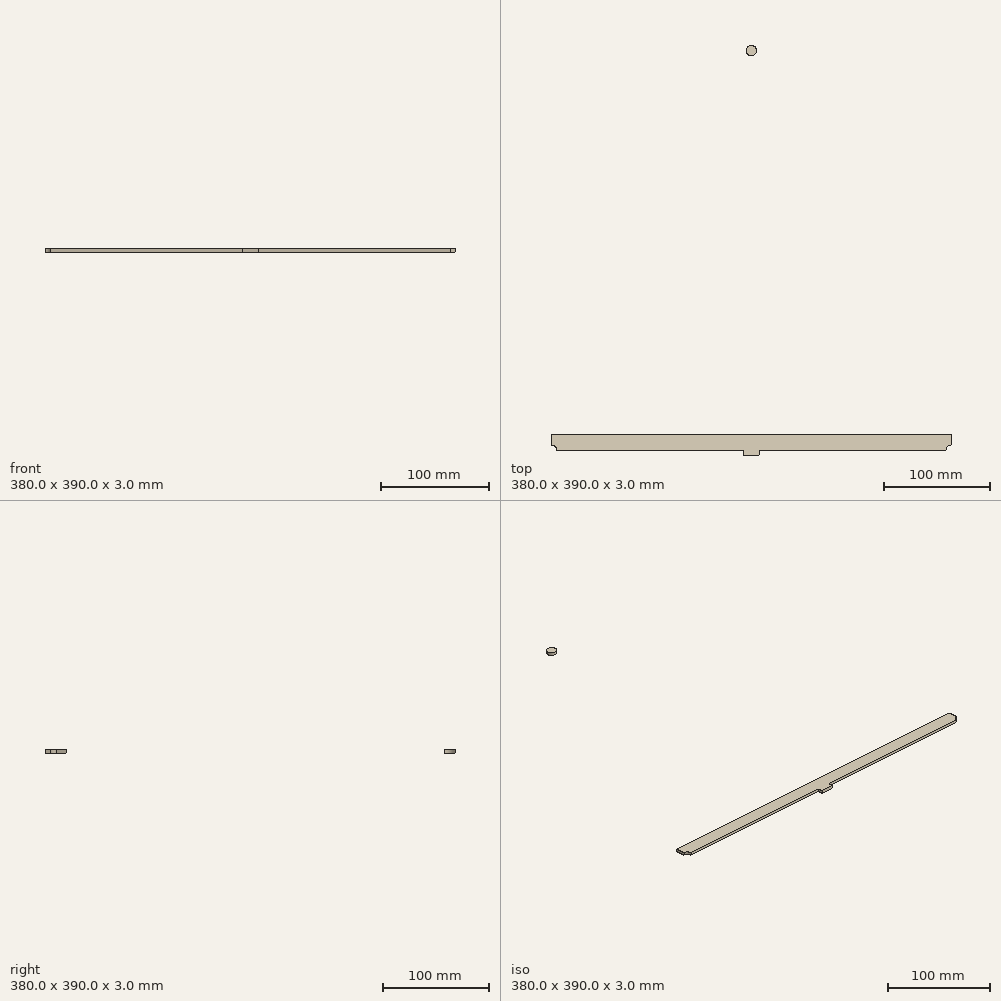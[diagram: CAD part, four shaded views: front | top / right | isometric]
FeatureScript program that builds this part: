
annotation { "Feature Type Name" : "Feature", "Feature Type Description" : "" }
export const myFeature = defineFeature(function(context is Context, id is Id, definition is map)
    precondition{}
    {
        {
            var Q0;
            Q0=qCreatedBy(makeId("Top.planeOp"),FACE);
            var sketch = newSketch(context, id + "F0", { "sketchPlane" : qUnion([Q0])});
            skLineSegment(sketch, "E0.bottom", {"start": v(240, -240) * mm, "end": v(-240, -240) * mm});
            skLineSegment(sketch, "E0.top", {"start": v(240, 240) * mm, "end": v(-240, 240) * mm});
            skLineSegment(sketch, "E0.left", {"start": v(240, -240) * mm, "end": v(240, 240) * mm});
            skLineSegment(sketch, "E0.right", {"start": v(-240, -240) * mm, "end": v(-240, 240) * mm});
            skPoint(sketch, "E0.middle", {"position": v(0, 0) * mm});
            skSolve(sketch);
        }
        {
            var Q0;
            Q0=makeQuery(id+"F0.imprint","IMPRINT",FACE,{"disambiguationData":[TD([[makeQuery(id+"F0.imprint","IMPRINT",EDGE,{"derivedFrom":sQuery(id+"F0.wireOp",EDGE,"E0.bottom")}),-1.0]])]});
            extrude(context, id + "F1", {"entities" : qUnion([Q0]), "depth" : 3 * mm, "offsetDistance" : 25 * mm});
        }
        {
            var Q0;
            Q0=makeQuery(id+"F1.opExtrude","CAP_FACE",FACE,{"disambiguationData":[OSD([sQuery(id+"F0.wireOp",EDGE,"E0.bottom"),sQuery(id+"F0.wireOp",EDGE,"E0.top"),sQuery(id+"F0.wireOp",EDGE,"E0.left"),sQuery(id+"F0.wireOp",EDGE,"E0.right")])],"isStart":false});
            var sketch = newSketch(context, id + "F2", { "sketchPlane" : qUnion([Q0])});
            skLineSegment(sketch, "E1.bottom", {"start": v(-240, 240) * mm, "end": v(-200, 240) * mm});
            skLineSegment(sketch, "E1.top", {"start": v(-240, 200) * mm, "end": v(-200, 200) * mm});
            skLineSegment(sketch, "E1.left", {"start": v(-240, 240) * mm, "end": v(-240, 200) * mm});
            skLineSegment(sketch, "E1.right", {"start": v(-200, 240) * mm, "end": v(-200, 200) * mm});
            skLineSegment(sketch, "E2.bottom", {"start": v(240, 240) * mm, "end": v(200, 240) * mm});
            skLineSegment(sketch, "E2.top", {"start": v(240, 200) * mm, "end": v(200, 200) * mm});
            skLineSegment(sketch, "E2.left", {"start": v(240, 240) * mm, "end": v(240, 200) * mm});
            skLineSegment(sketch, "E2.right", {"start": v(200, 240) * mm, "end": v(200, 200) * mm});
            skLineSegment(sketch, "E3.bottom", {"start": v(240, -240) * mm, "end": v(200, -240) * mm});
            skLineSegment(sketch, "E3.top", {"start": v(240, -200) * mm, "end": v(200, -200) * mm});
            skLineSegment(sketch, "E3.left", {"start": v(240, -240) * mm, "end": v(240, -200) * mm});
            skLineSegment(sketch, "E3.right", {"start": v(200, -240) * mm, "end": v(200, -200) * mm});
            skLineSegment(sketch, "E4.bottom", {"start": v(-240, -240) * mm, "end": v(-200, -240) * mm});
            skLineSegment(sketch, "E4.top", {"start": v(-240, -200) * mm, "end": v(-200, -200) * mm});
            skLineSegment(sketch, "E4.left", {"start": v(-240, -240) * mm, "end": v(-240, -200) * mm});
            skLineSegment(sketch, "E4.right", {"start": v(-200, -240) * mm, "end": v(-200, -200) * mm});
            skSolve(sketch);
        }
        {
            var Q0;
            Q0=qSketchRegion(id+"F2",true);
            extrude(context, id + "F3", {"entities" : qUnion([Q0]), "operationType" : NewBodyOperationType.REMOVE, "oppositeDirection" : true, "depth" : 25 * mm, "offsetDistance" : 25 * mm});
        }
        {
            var Q0;
            Q0=makeQuery(id+"F1.opExtrude","CAP_FACE",FACE,{"disambiguationData":[OSD([sQuery(id+"F0.wireOp",EDGE,"E0.bottom"),sQuery(id+"F0.wireOp",EDGE,"E0.top"),sQuery(id+"F0.wireOp",EDGE,"E0.left"),sQuery(id+"F0.wireOp",EDGE,"E0.right")])],"isStart":false});
            var sketch = newSketch(context, id + "F4", { "sketchPlane" : qUnion([Q0])});
            skLineSegment(sketch, "E5.bottom", {"start": v(-190, -190) * mm, "end": v(190, -190) * mm});
            skLineSegment(sketch, "E5.top", {"start": v(-190, 190) * mm, "end": v(190, 190) * mm});
            skLineSegment(sketch, "E5.left", {"start": v(-190, -190) * mm, "end": v(-190, 190) * mm});
            skLineSegment(sketch, "E5.right", {"start": v(190, -190) * mm, "end": v(190, 190) * mm});
            skPoint(sketch, "E6", {"position": v(0, 190) * mm});
            skPoint(sketch, "E7", {"position": v(-190, -190) * mm});
            skPoint(sketch, "E8", {"position": v(190, -190) * mm});
            skCircle(sketch, "E9", {"center": v(0, 190) * mm, "radius": 5 * mm});
            skCircle(sketch, "E10", {"center": v(-190, -190) * mm, "radius": 5 * mm});
            skCircle(sketch, "E11", {"center": v(190, -190) * mm, "radius": 5 * mm});
            skPoint(sketch, "E12", {"position": v(0, -190) * mm});
            skLineSegment(sketch, "E13.bottom", {"start": v(7.5, -190) * mm, "end": v(-7.5, -190) * mm});
            skLineSegment(sketch, "E13.top", {"start": v(7.5, -190) * mm, "end": v(-7.5, -190) * mm});
            skLineSegment(sketch, "E13.left", {"start": v(7.5, -190) * mm, "end": v(7.5, -190) * mm});
            skLineSegment(sketch, "E13.right", {"start": v(-7.5, -190) * mm, "end": v(-7.5, -190) * mm});
            skPoint(sketch, "E14", {"position": v(-7.5, -190) * mm});
            skPoint(sketch, "E15", {"position": v(7.5, -190) * mm});
            skLineSegment(sketch, "E16.bottom", {"start": v(-7.5, -190) * mm, "end": v(7.5, -190) * mm});
            skLineSegment(sketch, "E16.top", {"start": v(-7.5, -195) * mm, "end": v(7.5, -195) * mm});
            skLineSegment(sketch, "E16.left", {"start": v(-7.5, -190) * mm, "end": v(-7.5, -195) * mm});
            skLineSegment(sketch, "E16.right", {"start": v(7.5, -190) * mm, "end": v(7.5, -195) * mm});
            skLineSegment(sketch, "E17.bottom", {"start": v(200, -175) * mm, "end": v(-200, -175) * mm});
            skLineSegment(sketch, "E17.top", {"start": v(200, 175) * mm, "end": v(-200, 175) * mm});
            skLineSegment(sketch, "E17.left", {"start": v(200, -175) * mm, "end": v(200, 175) * mm});
            skLineSegment(sketch, "E17.right", {"start": v(-200, -175) * mm, "end": v(-200, 175) * mm});
            skPoint(sketch, "E17.middle", {"position": v(0, 0) * mm});
            skSolve(sketch);
        }
        {
            var Q0;
            {var subQ0=sQuery(id+"F4.wireOp",EDGE,"E9");var subQ1=sQuery(id+"F4.wireOp",EDGE,"E5.top");var subQ2=makeQuery(id+"F4.imprint","INTERSECT",VERTEX,{"disambiguationData":[OD(0.0)],"derivedFrom":[subQ1,subQ0]});Q0=makeQuery(id+"F4.imprint","IMPRINT",FACE,{"disambiguationData":[TD([[makeQuery(id+"F4.imprint","IMPRINT",EDGE,{"disambiguationData":[TD([[subQ2,-1.0]])],"derivedFrom":subQ1}),-1.0]])]});}
            var Q1;
            {var subQ0=sQuery(id+"F4.wireOp",EDGE,"E9");var subQ1=sQuery(id+"F4.wireOp",EDGE,"E5.top");var subQ2=makeQuery(id+"F4.imprint","INTERSECT",VERTEX,{"disambiguationData":[OD(0.0)],"derivedFrom":[subQ1,subQ0]});Q1=makeQuery(id+"F4.imprint","IMPRINT",FACE,{"disambiguationData":[TD([[makeQuery(id+"F4.imprint","IMPRINT",EDGE,{"disambiguationData":[TD([[subQ2,-1.0]])],"derivedFrom":subQ1}),1.0]])]});}
            var Q2;
            {var subQ0=sQuery(id+"F4.wireOp",EDGE,"E5.left");var subQ1=sQuery(id+"F4.wireOp",EDGE,"E5.bottom");var subQ2=makeQuery(id+"F4.imprint","INTERSECT",VERTEX,{"derivedFrom":[subQ1,subQ0]});Q2=makeQuery(id+"F4.imprint","IMPRINT",FACE,{"disambiguationData":[TD([[makeQuery(id+"F4.imprint","IMPRINT",EDGE,{"disambiguationData":[TD([[subQ2,-1.0]])],"derivedFrom":subQ1}),-1.0]])]});}
            var Q3;
            {var subQ0=sQuery(id+"F4.wireOp",EDGE,"E5.left");var subQ1=sQuery(id+"F4.wireOp",EDGE,"E5.bottom");var subQ2=makeQuery(id+"F4.imprint","INTERSECT",VERTEX,{"derivedFrom":[subQ1,subQ0]});Q3=makeQuery(id+"F4.imprint","IMPRINT",FACE,{"disambiguationData":[TD([[makeQuery(id+"F4.imprint","IMPRINT",EDGE,{"disambiguationData":[TD([[subQ2,-1.0]])],"derivedFrom":subQ1}),1.0]])]});}
            var Q4;
            {var subQ0=sQuery(id+"F4.wireOp",EDGE,"E5.right");var subQ1=sQuery(id+"F4.wireOp",EDGE,"E5.bottom");var subQ2=makeQuery(id+"F4.imprint","INTERSECT",VERTEX,{"derivedFrom":[subQ1,subQ0]});Q4=makeQuery(id+"F4.imprint","IMPRINT",FACE,{"disambiguationData":[TD([[makeQuery(id+"F4.imprint","IMPRINT",EDGE,{"disambiguationData":[TD([[subQ2,1.0]])],"derivedFrom":subQ1}),1.0]])]});}
            var Q5;
            {var subQ0=sQuery(id+"F4.wireOp",EDGE,"E5.right");var subQ1=sQuery(id+"F4.wireOp",EDGE,"E5.bottom");var subQ2=makeQuery(id+"F4.imprint","INTERSECT",VERTEX,{"derivedFrom":[subQ1,subQ0]});Q5=makeQuery(id+"F4.imprint","IMPRINT",FACE,{"disambiguationData":[TD([[makeQuery(id+"F4.imprint","IMPRINT",EDGE,{"disambiguationData":[TD([[subQ2,1.0]])],"derivedFrom":subQ1}),-1.0]])]});}
            var Q6;
            Q6=makeQuery(id+"F4.imprint","IMPRINT",FACE,{"disambiguationData":[TD([[makeQuery(id+"F4.imprint","IMPRINT",EDGE,{"derivedFrom":sQuery(id+"F4.wireOp",EDGE,"E17.bottom")}),-1.0]])]});
            extrude(context, id + "F5", {"entities" : qUnion([Q0, Q1, Q2, Q3, Q4, Q5, Q6]), "operationType" : NewBodyOperationType.REMOVE, "oppositeDirection" : true, "depth" : 25 * mm, "offsetDistance" : 25 * mm});
        }
    });
